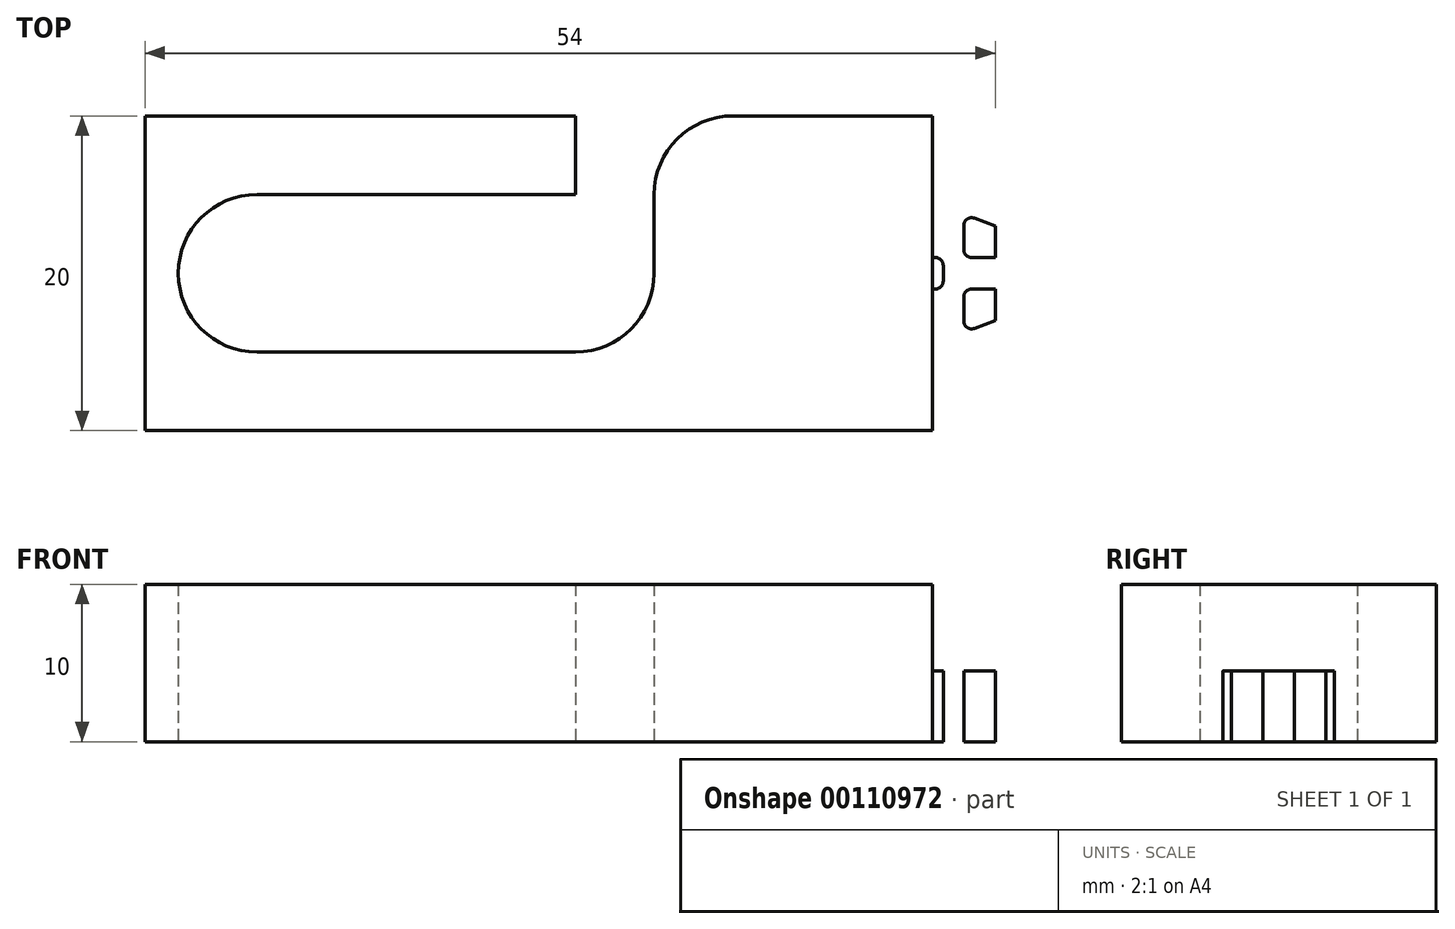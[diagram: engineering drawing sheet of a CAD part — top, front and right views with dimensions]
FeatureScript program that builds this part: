
annotation { "Feature Type Name" : "Feature", "Feature Type Description" : "" }
export const myFeature = defineFeature(function(context is Context, id is Id, definition is map)
    precondition{}
    {
        {
            var Q0;
            Q0=qCreatedBy(makeId("Top.planeOp"),FACE);
            var sketch = newSketch(context, id + "F0", { "sketchPlane" : qUnion([Q0])});
            skLineSegment(sketch, "E0.bottom", {"start": v(-10.94, 0) * mm, "end": v(39.06, 0) * mm});
            skLineSegment(sketch, "E0.top", {"start": v(-10.94, 20) * mm, "end": v(39.06, 20) * mm});
            skLineSegment(sketch, "E0.left", {"start": v(-10.94, 0) * mm, "end": v(-10.94, 20) * mm});
            skLineSegment(sketch, "E0.right", {"start": v(39.06, 0) * mm, "end": v(39.06, 20) * mm});
            skLineSegment(sketch, "E1.bottom", {"start": v(-8.83, 15) * mm, "end": v(21.4, 15) * mm});
            skLineSegment(sketch, "E1.top", {"start": v(-8.83, 5) * mm, "end": v(21.4, 5) * mm});
            skLineSegment(sketch, "E1.left", {"start": v(-8.83, 15) * mm, "end": v(-8.83, 5) * mm});
            skLineSegment(sketch, "E1.right", {"start": v(21.4, 15) * mm, "end": v(21.4, 5) * mm});
            skLineSegment(sketch, "E2", {"start": v(5.68, 0) * mm, "end": v(5.68, 5) * mm});
            skLineSegment(sketch, "E3", {"start": v(5.68, 15) * mm, "end": v(5.68, 20) * mm});
            skLineSegment(sketch, "E4.bottom", {"start": v(21.4, 15) * mm, "end": v(16.4, 15) * mm});
            skLineSegment(sketch, "E4.top", {"start": v(21.4, 20) * mm, "end": v(16.4, 20) * mm});
            skLineSegment(sketch, "E4.left", {"start": v(21.4, 15) * mm, "end": v(21.4, 20) * mm});
            skLineSegment(sketch, "E4.right", {"start": v(16.4, 15) * mm, "end": v(16.4, 20) * mm});
            skPoint(sketch, "E5", {"position": v(21.4, 10) * mm});
            skLineSegment(sketch, "E6.bottom", {"start": v(39.06, 13) * mm, "end": v(43.06, 13) * mm});
            skLineSegment(sketch, "E6.top", {"start": v(39.06, 11) * mm, "end": v(43.06, 11) * mm});
            skLineSegment(sketch, "E6.left", {"start": v(39.06, 13) * mm, "end": v(39.06, 11) * mm});
            skLineSegment(sketch, "E6.right", {"start": v(43.06, 13) * mm, "end": v(43.06, 11) * mm});
            skLineSegment(sketch, "E7.bottom", {"start": v(39.06, 7) * mm, "end": v(43.06, 7) * mm});
            skLineSegment(sketch, "E7.top", {"start": v(39.06, 9) * mm, "end": v(43.06, 9) * mm});
            skLineSegment(sketch, "E7.left", {"start": v(39.06, 7) * mm, "end": v(39.06, 9) * mm});
            skLineSegment(sketch, "E7.right", {"start": v(43.06, 7) * mm, "end": v(43.06, 9) * mm});
            skLineSegment(sketch, "E8", {"start": v(43.06, 13) * mm, "end": v(41.06, 13.75) * mm});
            skLineSegment(sketch, "E9", {"start": v(41.06, 13.75) * mm, "end": v(41.06, 6.25) * mm});
            skLineSegment(sketch, "E10", {"start": v(41.06, 6.25) * mm, "end": v(43.06, 7) * mm});
            skPoint(sketch, "E11", {"position": v(41.06, 10) * mm});
            skPoint(sketch, "E12", {"position": v(39.06, 10) * mm});
            skLineSegment(sketch, "E13", {"start": v(39.76, 11) * mm, "end": v(39.76, 9) * mm});
            skSolve(sketch);
        }
        {
            var Q0;
            {var subQ3=sQuery(id+"F0.wireOp",EDGE,"E0.left");Q0=makeQuery(id+"F0.imprint","IMPRINT",FACE,{"disambiguationData":[TD([[makeQuery(id+"F0.imprint","IMPRINT",EDGE,{"derivedFrom":subQ3}),-1.0]])]});}
            var Q1;
            {var subQ3=sQuery(id+"F0.wireOp",EDGE,"E0.right");Q1=makeQuery(id+"F0.imprint","IMPRINT",FACE,{"disambiguationData":[TD([[makeQuery(id+"F0.imprint","IMPRINT",EDGE,{"derivedFrom":subQ3}),1.0]])]});}
            var Q2;
            {var subQ0=sQuery(id+"F0.wireOp",EDGE,"E3");Q2=makeQuery(id+"F0.imprint","IMPRINT",FACE,{"disambiguationData":[TD([[makeQuery(id+"F0.imprint","IMPRINT",EDGE,{"derivedFrom":subQ0}),-1.0]])]});}
            extrude(context, id + "F1", {"entities" : qUnion([Q0, Q1, Q2]), "depth" : 10 * mm});
        }
        {
            var Q0;
            {var subQ0=sQuery(id+"F0.wireOp",EDGE,"E7.left");Q0=makeQuery(id+"F0.imprint","IMPRINT",FACE,{"disambiguationData":[TD([[makeQuery(id+"F0.imprint","IMPRINT",EDGE,{"derivedFrom":subQ0}),-1.0]])]});}
            var Q1;
            {var subQ0=sQuery(id+"F0.wireOp",EDGE,"E7.right");Q1=makeQuery(id+"F0.imprint","IMPRINT",FACE,{"disambiguationData":[TD([[makeQuery(id+"F0.imprint","IMPRINT",EDGE,{"derivedFrom":subQ0}),1.0]])]});}
            var Q2;
            {var subQ0=sQuery(id+"F0.wireOp",EDGE,"E10");Q2=makeQuery(id+"F0.imprint","IMPRINT",FACE,{"disambiguationData":[TD([[makeQuery(id+"F0.imprint","IMPRINT",EDGE,{"derivedFrom":subQ0}),1.0]])]});}
            var Q3;
            {var subQ0=sQuery(id+"F0.wireOp",EDGE,"E6.left");Q3=makeQuery(id+"F0.imprint","IMPRINT",FACE,{"disambiguationData":[TD([[makeQuery(id+"F0.imprint","IMPRINT",EDGE,{"derivedFrom":subQ0}),1.0]])]});}
            var Q4;
            {var subQ0=sQuery(id+"F0.wireOp",EDGE,"E6.right");Q4=makeQuery(id+"F0.imprint","IMPRINT",FACE,{"disambiguationData":[TD([[makeQuery(id+"F0.imprint","IMPRINT",EDGE,{"derivedFrom":subQ0}),-1.0]])]});}
            var Q5;
            {var subQ0=sQuery(id+"F0.wireOp",EDGE,"E8");Q5=makeQuery(id+"F0.imprint","IMPRINT",FACE,{"disambiguationData":[TD([[makeQuery(id+"F0.imprint","IMPRINT",EDGE,{"derivedFrom":subQ0}),1.0]])]});}
            var Q6;
            {var subQ5=sQuery(id+"F0.wireOp",EDGE,"E13");Q6=makeQuery(id+"F0.imprint","IMPRINT",FACE,{"disambiguationData":[TD([[makeQuery(id+"F0.imprint","IMPRINT",EDGE,{"derivedFrom":subQ5}),-1.0]])]});}
            extrude(context, id + "F2", {"entities" : qUnion([Q0, Q1, Q2, Q3, Q4, Q5, Q6]), "operationType" : NewBodyOperationType.ADD, "depth" : 4.5 * mm});
        }
        {
            var Q0;
            Q0=makeQuery(id+"FwrvMl2xzgpzGwf_1.opExtrude","CAP_EDGE",EDGE,{"disambiguationData":[OSD([sQuery(id+"F4PTOhtl7EFL90g_1.wireOp",EDGE,"oZkCBkvO-QUaH-s3bU-aoQX-DPy4y0Fgcs5u.top")])],"isStart":false});
            var Q1;
            Q1=makeQuery(id+"FwrvMl2xzgpzGwf_1.opExtrude","CAP_EDGE",EDGE,{"disambiguationData":[OSD([sQuery(id+"F4PTOhtl7EFL90g_1.wireOp",EDGE,"oZkCBkvO-QUaH-s3bU-aoQX-DPy4y0Fgcs5u.bottom")])],"isStart":false});
            var Q2;
            Q2=makeQuery(id+"F1.opExtrude","SWEPT_EDGE",EDGE,{"disambiguationData":[OSD([sQuery(id+"F0.wireOp",EDGE,"E1.bottom"),sQuery(id+"F0.wireOp",EDGE,"E1.left")])]});
            var Q3;
            Q3=makeQuery(id+"F1.opExtrude","SWEPT_EDGE",EDGE,{"disambiguationData":[OSD([sQuery(id+"F0.wireOp",EDGE,"E1.top"),sQuery(id+"F0.wireOp",EDGE,"E1.left")])]});
            var Q4;
            Q4=makeQuery(id+"F1.opExtrude","SWEPT_EDGE",EDGE,{"disambiguationData":[OSD([sQuery(id+"F0.wireOp",EDGE,"E1.top"),sQuery(id+"F0.wireOp",EDGE,"E1.right")])]});
            var Q5;
            Q5=makeQuery(id+"F1.opExtrude","SWEPT_EDGE",EDGE,{"disambiguationData":[OSD([sQuery(id+"F0.wireOp",EDGE,"E0.top"),sQuery(id+"F0.wireOp",EDGE,"E4.top"),sQuery(id+"F0.wireOp",EDGE,"E4.left")])]});
            fillet(context, id + "F3", {"entities" : qUnion([Q0, Q1, Q2, Q3, Q4, Q5]), "radius" : 5 * mm, "tangentPropagation" : true, "allowEdgeOverflow" : false});
        }
        {
            var Q0;
            Q0=makeQuery(id+"F2.opExtrude","SWEPT_EDGE",EDGE,{"disambiguationData":[OSD([sQuery(id+"F0.wireOp",EDGE,"E0.right"),sQuery(id+"F0.wireOp",EDGE,"E6.top"),sQuery(id+"F0.wireOp",EDGE,"E6.left")])]});
            var Q1;
            Q1=makeQuery(id+"F2.opExtrude","SWEPT_EDGE",EDGE,{"disambiguationData":[OSD([sQuery(id+"F0.wireOp",EDGE,"E0.right"),sQuery(id+"F0.wireOp",EDGE,"E7.top"),sQuery(id+"F0.wireOp",EDGE,"E7.left")])]});
            var Q2;
            Q2=makeQuery(id+"F2.opExtrude","SWEPT_EDGE",EDGE,{"disambiguationData":[OSD([sQuery(id+"F0.wireOp",EDGE,"E0.right"),sQuery(id+"F0.wireOp",EDGE,"E6.bottom"),sQuery(id+"F0.wireOp",EDGE,"E6.left")])]});
            var Q3;
            Q3=makeQuery(id+"F2.opExtrude","SWEPT_EDGE",EDGE,{"disambiguationData":[OSD([sQuery(id+"F0.wireOp",EDGE,"E0.right"),sQuery(id+"F0.wireOp",EDGE,"E7.bottom"),sQuery(id+"F0.wireOp",EDGE,"E7.left")])]});
            var Q4;
            Q4=makeQuery(id+"F2.opExtrude","SWEPT_EDGE",EDGE,{"disambiguationData":[OSD([sQuery(id+"F0.wireOp",EDGE,"E7.bottom"),sQuery(id+"F0.wireOp",EDGE,"E9")])]});
            var Q5;
            Q5=makeQuery(id+"F2.opExtrude","SWEPT_EDGE",EDGE,{"disambiguationData":[OSD([sQuery(id+"F0.wireOp",EDGE,"E6.bottom"),sQuery(id+"F0.wireOp",EDGE,"E9")])]});
            var Q6;
            Q6=makeQuery(id+"F2.opExtrude","SWEPT_EDGE",EDGE,{"disambiguationData":[OSD([sQuery(id+"F0.wireOp",EDGE,"E6.top"),sQuery(id+"F0.wireOp",EDGE,"E13")])]});
            var Q7;
            Q7=makeQuery(id+"F2.opExtrude","SWEPT_EDGE",EDGE,{"disambiguationData":[OSD([sQuery(id+"F0.wireOp",EDGE,"E7.top"),sQuery(id+"F0.wireOp",EDGE,"E13")])]});
            fillet(context, id + "F4", {"entities" : qUnion([Q0, Q1, Q2, Q3, Q4, Q5, Q6, Q7]), "radius" : 0.5 * mm, "tangentPropagation" : true, "allowEdgeOverflow" : false});
        }
    });
